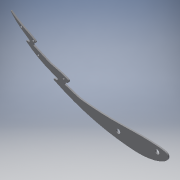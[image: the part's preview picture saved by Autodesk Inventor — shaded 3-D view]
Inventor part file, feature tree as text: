
AUTODESK INVENTOR PART (.ipt)
format: ipt  version: 2018 (Build 220112000, 112)  size: 196,096 bytes
history: native  units: mm
features: other x4, extrude x3, sketch x3, reference x2
ambient origin geometry x8: Origin, YZ Plane, XZ Plane, XY Plane, X Axis, Y Axis, Z Axis, Center Point
bodies: Body1 (feature_tree)
feature tree (12):
  extrude  "押し出し2"  Depth=4.0mm
  extrude  "押し出し3"  Depth=4.0mm TaperAngle=0.0deg
  extrude  "押し出し4"  Depth=6.5mm
  sketch  "スケッチ1"
  sketch  "スケッチ2"
  sketch  "スケッチ3"
  reference  "参照1"
  reference  "参照2"
  parser-record x1  (decoder bookkeeping rows leaked as tree rows — omitted from the tree; the rows remain in map.json)
  other  "Fr.wing_assy.iam"
  other  "axis_f2:4"
  other  "axis_f2:3"
note: 1 file-system path scrubbed to <path> (originals preserved in map.json)
